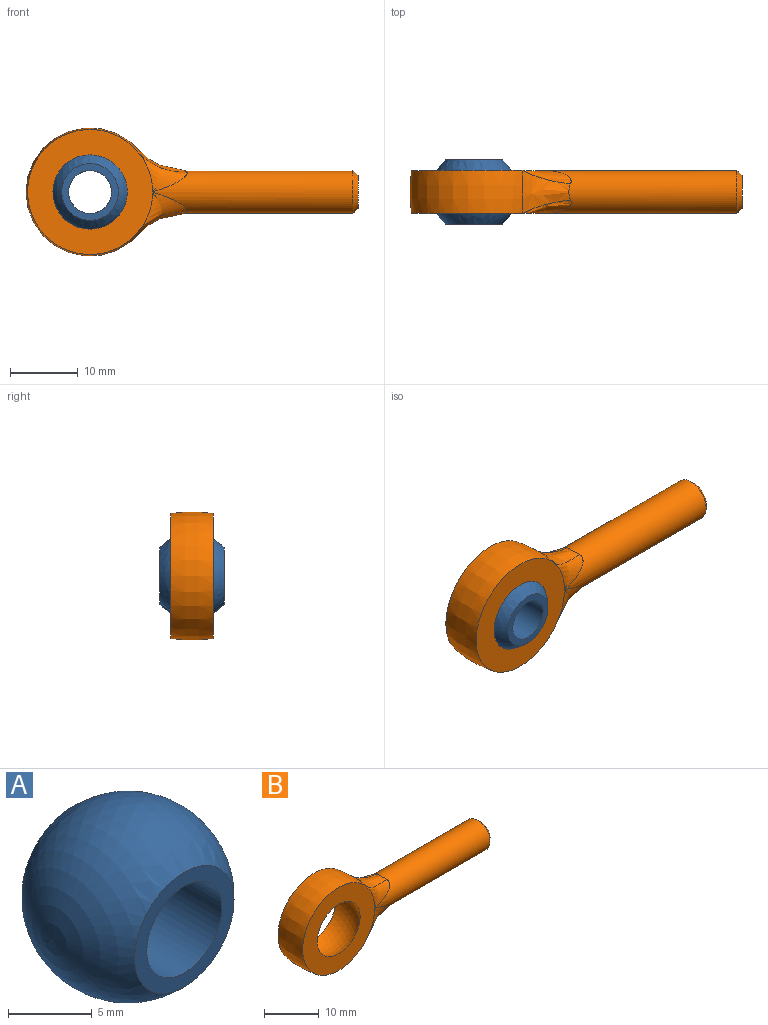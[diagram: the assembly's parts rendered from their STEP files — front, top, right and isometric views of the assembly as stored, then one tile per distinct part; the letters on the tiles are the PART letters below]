
ASSEMBLY  parts=2 mates=1
PART A: 4 faces, bbox 12.7x12.7x12.7 mm
  f0: sphere r=6.35mm, area 380mm2, adj f1,f2
  f1: plane 8.4x8.4mm, normal (0,1,0), area 23.8mm2, adj f0,f3
  f2: plane 8.4x8.4mm, normal (0,-1,0), area 23.8mm2, adj f0,f3
  f3: cylinder r=3.17mm len=9.53mm, axis (0,-1,0), area 190mm2, adj f1,f2
PART B: 13 faces, bbox 49.2x9.7x19 mm
  f0: revolved ~19.04x16.97mm, area 293.4mm2, adj f1,f2,f7,f10
  f1: plane 18.52x18.52mm, normal (0,1,0), area 174.3mm2, adj f0,f3,f8,f9
  f2: plane 18.52x18.52mm, normal (0,-1,0), area 174.3mm2, adj f0,f3,f6,f11
  f3: sphere r=6.35mm, area 253.4mm2, adj f1,f2
  f4: plane 4.83x4.83mm, normal (1,0,0), area 18.3mm2, adj f12
  f5: cylinder r=3.17mm len=29.67mm, axis (1,0,0), area 513.4mm2, adj f6,f7,f8,f9,f10,f11,f12
  f6: bspline ~7.37x6.06mm, area 17mm2, adj f2,f5,f7
  f7: bspline ~9.65x7.48mm, area 32.7mm2, adj f0,f5,f6,f8
  f8: bspline ~7.37x6.06mm, area 17mm2, adj f1,f5,f7
  f9: bspline ~7.37x6.06mm, area 17mm2, adj f1,f5,f10
  f10: bspline ~9.65x7.48mm, area 32.7mm2, adj f0,f5,f9,f11
  f11: bspline ~7.37x6.06mm, area 17mm2, adj f2,f5,f10
  f12: cone r=2.41mm half-angle=45deg, axis (-1,0,0), area 18.9mm2, adj f4,f5
PLACE A at identity
PLACE B at identity fixed
MATE ball A.f3 <-> B.f0  axis (0,-1,0) through (0,0,0)mm
